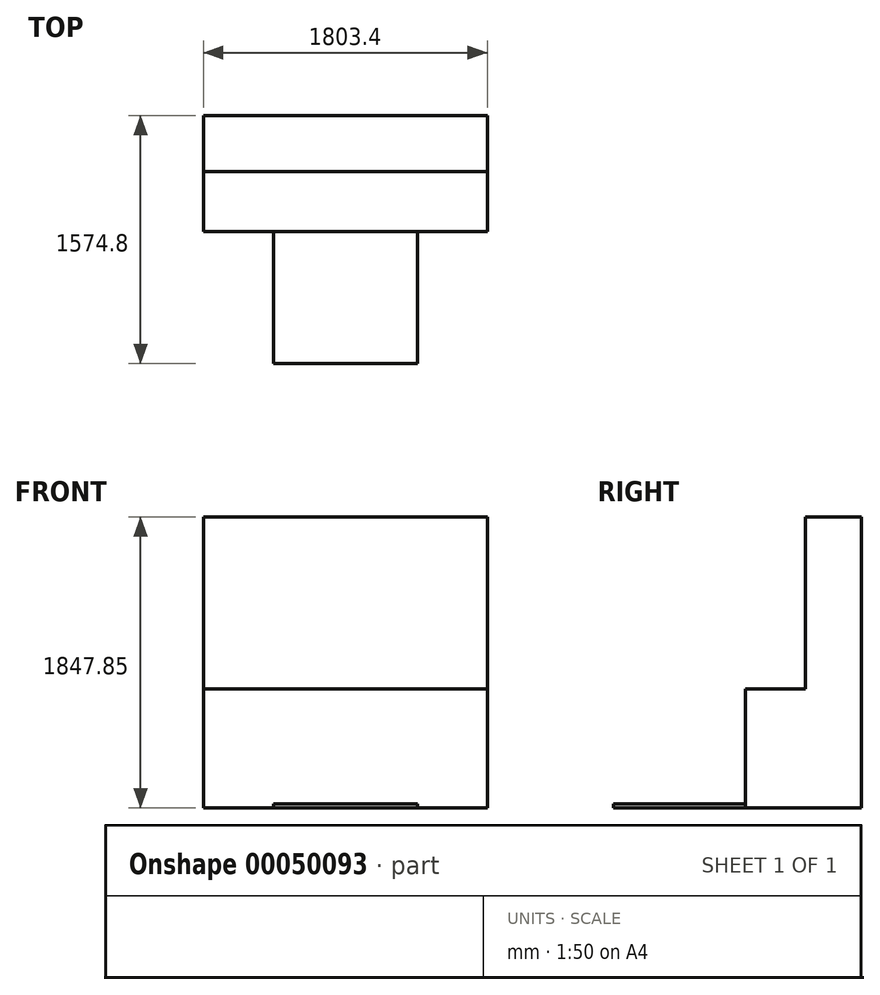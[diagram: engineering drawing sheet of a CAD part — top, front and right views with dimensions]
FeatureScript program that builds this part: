
annotation { "Feature Type Name" : "Feature", "Feature Type Description" : "" }
export const myFeature = defineFeature(function(context is Context, id is Id, definition is map)
    precondition{}
    {
        {
            var Q0;
            Q0=qCreatedBy(makeId("Top.planeOp"),FACE);
            var sketch = newSketch(context, id + "F0", { "sketchPlane" : qUnion([Q0])});
            skLineSegment(sketch, "E0.bottom", {"start": v(-901.7, 368.3) * mm, "end": v(901.7, 368.3) * mm});
            skLineSegment(sketch, "E0.top", {"start": v(-901.7, -368.3) * mm, "end": v(901.7, -368.3) * mm});
            skLineSegment(sketch, "E0.left", {"start": v(-901.7, 368.3) * mm, "end": v(-901.7, -368.3) * mm});
            skLineSegment(sketch, "E0.right", {"start": v(901.7, 368.3) * mm, "end": v(901.7, -368.3) * mm});
            skSolve(sketch);
        }
        {
            var Q0;
            Q0=qCreatedBy(makeId("Top.planeOp"),FACE);
            var sketch = newSketch(context, id + "F1", { "sketchPlane" : qUnion([Q0])});
            skLineSegment(sketch, "E1.bottom", {"start": v(-457.2, -368.3) * mm, "end": v(457.2, -368.3) * mm});
            skLineSegment(sketch, "E1.top", {"start": v(-457.2, -1206.5) * mm, "end": v(457.2, -1206.5) * mm});
            skLineSegment(sketch, "E1.left", {"start": v(-457.2, -368.3) * mm, "end": v(-457.2, -1206.5) * mm});
            skLineSegment(sketch, "E1.right", {"start": v(457.2, -368.3) * mm, "end": v(457.2, -1206.5) * mm});
            skSolve(sketch);
        }
        {
            var Q0;
            Q0 = qSketchRegion(id + "F0", true);
            extrude(context, id + "F2", {"entities" : qUnion([Q0]), "depth" : 755.65 * mm});
        }
        {
            var Q0;
            Q0 = qSketchRegion(id + "F1", true);
            extrude(context, id + "F3", {"entities" : qUnion([Q0]), "operationType" : NewBodyOperationType.ADD, "depth" : 25.4 * mm});
        }
        {
            var Q0;
            Q0=makeQuery(id+"F2.opExtrude","CAP_FACE",FACE,{"disambiguationData":[OSD([sQuery(id+"F0.wireOp",EDGE,"E0.bottom"),sQuery(id+"F0.wireOp",EDGE,"E0.top"),sQuery(id+"F0.wireOp",EDGE,"E0.left"),sQuery(id+"F0.wireOp",EDGE,"E0.right")])],"isStart":false});
            var sketch = newSketch(context, id + "F4", { "sketchPlane" : qUnion([Q0])});
            skLineSegment(sketch, "E2.bottom", {"start": v(-901.7, 368.3) * mm, "end": v(901.7, 368.3) * mm});
            skLineSegment(sketch, "E2.top", {"start": v(-901.7, 12.7) * mm, "end": v(901.7, 12.7) * mm});
            skLineSegment(sketch, "E2.left", {"start": v(-901.7, 368.3) * mm, "end": v(-901.7, 12.7) * mm});
            skLineSegment(sketch, "E2.right", {"start": v(901.7, 368.3) * mm, "end": v(901.7, 12.7) * mm});
            skSolve(sketch);
        }
        {
            var Q0;
            Q0 = qSketchRegion(id + "F4", true);
            extrude(context, id + "F5", {"entities" : qUnion([Q0]), "operationType" : NewBodyOperationType.ADD, "depth" : 1092.2 * mm});
        }
    });
